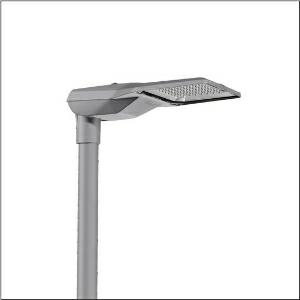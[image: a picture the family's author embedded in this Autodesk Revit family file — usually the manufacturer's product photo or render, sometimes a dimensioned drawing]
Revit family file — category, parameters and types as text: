
# Revit family: streetlight_sl_21_midi___stw1_0a_5xe3e33s08mb_c28b
name_source: partatom
category: Lighting Fixtures
units: mm (PartAtom-declared; Revit-internal decimal feet)

## family parameters
Cut with Voids When Loaded = No
Host = Face
Light Source = No
Part Type = Normal
Room Calculation Point = No
Round Connector Dimension = Use Diameter
Shared = No

## types (1)
- --- (1 x LED, 18270 lm, 136 W, 3000K)
    Apparent Load = 136 VA
    CIE Flux Codes = 38 75 98 100 100
    Color Rendering = 70
    Color Temperature = 3000K
    Default Elevation = 1800 mm
    Description = Streetlight SL 21 midi, mast luminaire, primary light control with lens, of PMMA, primary optical cover: cover, of toughened safety glass, transparent, light distribution: STW1.0a, light emission: direct distribution, primary light characteristic: asymmetric, installation type: side-entry, post-top, LED, High Power LED, rated luminous flux: 18.270lm, luminous efficacy: 134lm/W, light colour: 730, colour temperature: 3000K, control gear: D4i, control: overheat protection, constant luminous flux control, time-dependent luminous flux control, flexible luminous flux parameterisation, pre-setting: logarithmic dimming characteristic, mains connection: 230..240V, AC, 50/60Hz, start of lifetime: 136W, end of service life: 142W, reduction: 61W, luminaire housing, of diecast aluminium, powder-coated, Siteco® metallic grey (DB 702S), corrosivity category C5 mid according to DIN EN ISO 12944, please order mast flange separately, inclination adjustable: 0°, 5°, 10°, 15°, sealing non-destructively replaceable, multi-level sealing system, length: 644mm, width: 335mm, height: 110mm, mast flange for spigot size: 42mm (side-entry): 5XC10008XM4, 60/48mm (side-entry/post-top): 5XC10108XM2, 76/60mm (side-entry/post-top): 5XC10108XM1, mounting height: 4..8m, Smart Interface above, protection rating (complete): IP66, insulation class (complete): insulation class II (safety insulation), certification: CE, ENEC, ENEC+, VDE, impact resistance: IK10, permissible operating ambient temperature for outdoor applications: -40..+50°C, standard-compliant lighting for roads and squares, packaging unit: 1 piece

Light Distribution: STW1.0a
    Height = 111 mm
    Lamp = 1 x LED
    Lamp Light Flux = 18270 lm
    Lamp Power = 136 W
    Lamp count = 1
    Length = 644 mm
    Luminous efficacy = 134 lm/W
    Manufacturer = Siteco
    ModVariant = No
    Model = 5XE3E33S08MB
    Number of Poles = 1
    OnlyDefault = Yes
    Power Factor = 1
    Product Name = Streetlight SL 21 midi | STW1.0a
    Product group = mast luminaire | pylon top
    ProductGroupID = 6100
    Protection Class = Protection class II
    Protection Degree = IP 66
    RLX_Detail_Level = 1
    RLX_Emergency_Light_Flux = 0 lm
    RLX_Emergency_Type = 0
    RLX_Emergency_Type_DB = No
    RlxData = <blob elided: 26825 chars, md5=fa8c5878>
    Socket = socket
    Standby Power = 0 W
    System Light Flux = 18270 lm
    System Power = 136 W
    Type Comments = factory setting: luminous flux: 100 % | dim-lin: 254 | 695 mA
    Type Image = l_1004302.jpg
    URL = http://relux.com
    VarID = @adj_187984
    Voltage = 0 V
    Weight = 0.00 kg
    Width = 336 mm

## geometry (parser evidence)
native form markers: Blend x4, Sweep x12
no freeform markers — native parametric forms only
